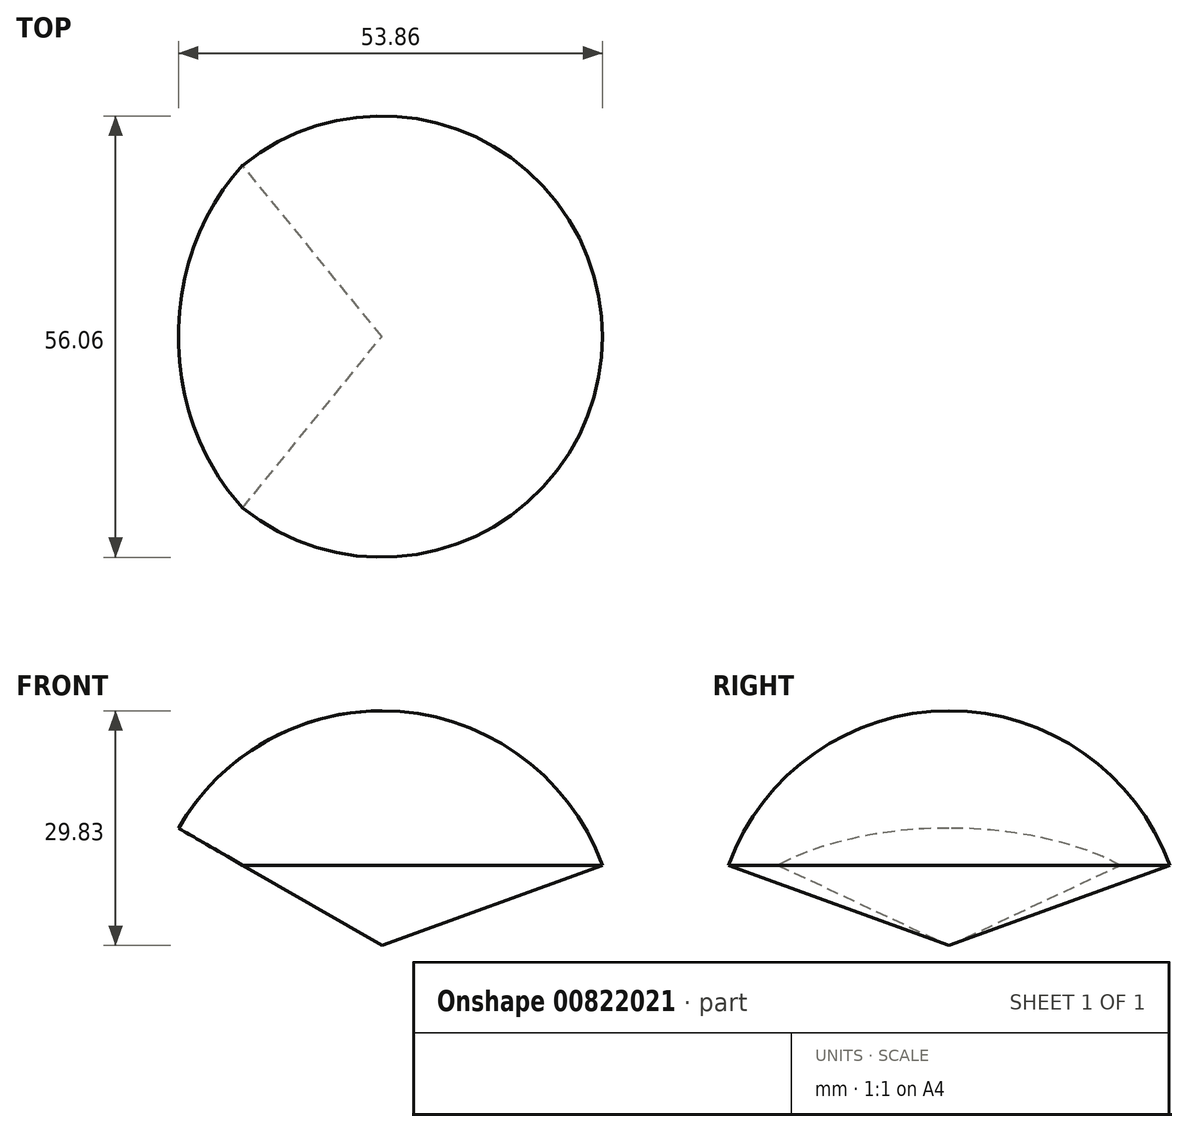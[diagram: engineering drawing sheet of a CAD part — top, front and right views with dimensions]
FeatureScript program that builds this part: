
annotation { "Feature Type Name" : "Feature", "Feature Type Description" : "" }
export const myFeature = defineFeature(function(context is Context, id is Id, definition is map)
    precondition{}
    {
        {
            var Q0;
            Q0=qCreatedBy(makeId("Front.planeOp"),FACE);
            var sketch = newSketch(context, id + "F0", { "sketchPlane" : qUnion([Q0])});
            skArc(sketch, "E0", {"start": v(-28.03, -10.2) * mm, "mid": v(29.83, 0) * mm, "end": v(-28.03, 10.2) * mm});
            skLineSegment(sketch, "E1", {"start": v(0, 0) * mm, "end": v(-28.03, 10.2) * mm});
            skLineSegment(sketch, "E2", {"start": v(0, 0) * mm, "end": v(-28.03, -10.2) * mm});
            skLineSegment(sketch, "E3", {"start": v(0, 0) * mm, "end": v(-29.83, 0) * mm, "construction": true});
            skLineSegment(sketch, "E4", {"start": v(0, 36.27) * mm, "end": v(0, -43.8) * mm, "construction": true});
            skLineSegment(sketch, "E5", {"start": v(0, -29.83) * mm, "end": v(0, 29.83) * mm});
            skSolve(sketch);
        }
        {
            var Q0;
            {var subQ0=sQuery(id+"F0.wireOp",EDGE,"E5");var subQ1=sQuery(id+"F0.wireOp",EDGE,"E0");var subQ2=makeQuery(id+"F0.imprint","INTERSECT",VERTEX,{"disambiguationData":[OD(0.0)],"derivedFrom":[subQ1,subQ0]});Q0=makeQuery(id+"F0.imprint","IMPRINT",FACE,{"disambiguationData":[TD([[makeQuery(id+"F0.imprint","IMPRINT",EDGE,{"disambiguationData":[TD([[subQ2,-1.0]])],"derivedFrom":subQ1}),1.0]])]});}
            var Q1;
            Q1=sQuery(id+"F0.wireOp",EDGE,"E4");
            revolve(context, id + "F1", {"surfaceOperationType" : NewSurfaceOperationType.NEW, "entities" : qUnion([Q0]), "axis" : qUnion([Q1]), "revolveType" : RevolveType.FULL});
        }
        {
            var Q0;
            Q0=qCreatedBy(makeId("Front.planeOp"),FACE);
            var sketch = newSketch(context, id + "F2", { "sketchPlane" : qUnion([Q0])});
            skLineSegment(sketch, "E6", {"start": v(0, 0) * mm, "end": v(-32.06, 18.5) * mm});
            skLineSegment(sketch, "E7", {"start": v(0, 0) * mm, "end": v(-32.5, -18.77) * mm});
            skLineSegment(sketch, "E8", {"start": v(-32.06, 18.5) * mm, "end": v(-32.5, -18.77) * mm});
            skLineSegment(sketch, "E9", {"start": v(0, 32.04) * mm, "end": v(0, -38.4) * mm, "construction": true});
            skSolve(sketch);
        }
        {
            var Q0;
            Q0 = qSketchRegion(id + "F2", true);
            extrude(context, id + "F3", {"entities" : qUnion([Q0]), "operationType" : NewBodyOperationType.REMOVE, "endBound" : BoundingType.SYMMETRIC, "oppositeDirection" : true, "depth" : 63.5 * mm, "offsetDistance" : 25.4 * mm});
        }
    });
